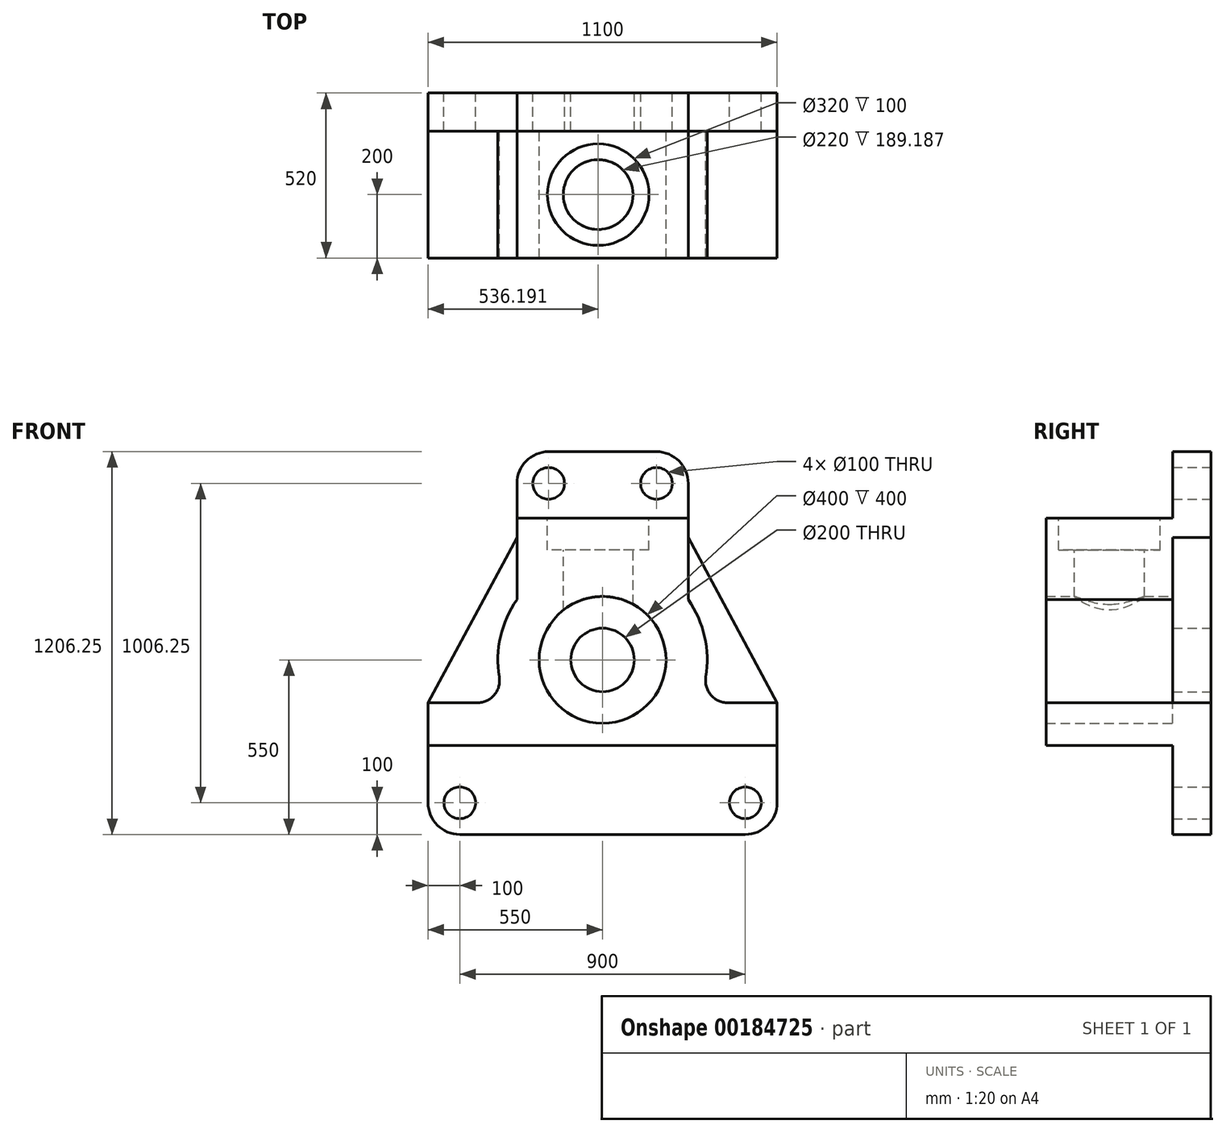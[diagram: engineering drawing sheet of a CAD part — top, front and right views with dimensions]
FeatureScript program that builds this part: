
annotation { "Feature Type Name" : "Feature", "Feature Type Description" : "" }
export const myFeature = defineFeature(function(context is Context, id is Id, definition is map)
    precondition{}
    {
        {
            var Q0;
            Q0=qCreatedBy(makeId("Front.planeOp"),FACE);
            var sketch = newSketch(context, id + "F0", { "sketchPlane" : qUnion([Q0])});
            skLineSegment(sketch, "E0", {"start": v(0, 1430) * mm, "end": v(0, -470) * mm, "construction": true});
            skLineSegment(sketch, "E1", {"start": v(450, 0) * mm, "end": v(60, 0) * mm});
            skLineSegment(sketch, "E2", {"start": v(-60, 0) * mm, "end": v(-60, 280) * mm});
            skLineSegment(sketch, "E3", {"start": v(60, 0) * mm, "end": v(60, 280) * mm});
            skArc(sketch, "E4", {"start": v(-450, 0) * mm, "mid": v(-520.71, 29.29) * mm, "end": v(-550, 100) * mm});
            skArc(sketch, "E5", {"start": v(450, 0) * mm, "mid": v(520.71, 29.29) * mm, "end": v(550, 100) * mm});
            skCircle(sketch, "E6", {"center": v(-450, 100) * mm, "radius": 50 * mm});
            skCircle(sketch, "E7", {"center": v(450, 100) * mm, "radius": 50 * mm});
            skLineSegment(sketch, "E8", {"start": v(-550, 100) * mm, "end": v(-550, 280) * mm});
            skLineSegment(sketch, "E9", {"start": v(550, 100) * mm, "end": v(550, 280) * mm});
            skLineSegment(sketch, "E10", {"start": v(-60, 280) * mm, "end": v(-550, 280) * mm});
            skLineSegment(sketch, "E11", {"start": v(60, 280) * mm, "end": v(550, 280) * mm});
            skLineSegment(sketch, "E12", {"start": v(-60, 280) * mm, "end": v(60, 280) * mm});
            skCircle(sketch, "E13", {"center": v(0, 550) * mm, "radius": 100 * mm});
            skCircle(sketch, "E14", {"center": v(0, 550) * mm, "radius": 200 * mm});
            skLineSegment(sketch, "E15", {"start": v(-550, 280) * mm, "end": v(-550, 415) * mm});
            skArc(sketch, "E16", {"start": v(325.61, 496.38) * mm, "mid": v(321.7, 623.52) * mm, "end": v(270, 739.74) * mm});
            skLineSegment(sketch, "E17", {"start": v(-550, 415) * mm, "end": v(-394.68, 415) * mm});
            skArc(sketch, "E18", {"start": v(-394.68, 415) * mm, "mid": v(-341.32, 439.7) * mm, "end": v(-325.61, 496.37) * mm});
            skLineSegment(sketch, "E19.MirrorCS", {"start": v(550, 280) * mm, "end": v(550, 415) * mm});
            skLineSegment(sketch, "E20.MirrorCS", {"start": v(550, 415) * mm, "end": v(394.68, 415) * mm});
            skArc(sketch, "E21.MirrorCS", {"start": v(394.68, 415) * mm, "mid": v(341.32, 439.7) * mm, "end": v(325.61, 496.37) * mm});
            skLineSegment(sketch, "E22", {"start": v(270, 996.25) * mm, "end": v(-270, 996.25) * mm});
            skArc(sketch, "E23", {"start": v(-170, 1206.25) * mm, "mid": v(-240.71, 1176.96) * mm, "end": v(-270, 1106.25) * mm});
            skArc(sketch, "E24.MirrorCS", {"start": v(170, 1206.25) * mm, "mid": v(240.71, 1176.96) * mm, "end": v(270, 1106.25) * mm});
            skLineSegment(sketch, "E25", {"start": v(-270, 1106.25) * mm, "end": v(-270, 996.25) * mm});
            skLineSegment(sketch, "E26", {"start": v(270, 1106.25) * mm, "end": v(270, 996.25) * mm});
            skCircle(sketch, "E27", {"center": v(-170, 1106.25) * mm, "radius": 50 * mm});
            skCircle(sketch, "E28.MirrorC", {"center": v(170, 1106.25) * mm, "radius": 50 * mm});
            skLineSegment(sketch, "E29", {"start": v(-270, 996.25) * mm, "end": v(-270, 739.74) * mm});
            skLineSegment(sketch, "E30", {"start": v(270, 996.25) * mm, "end": v(270, 739.74) * mm});
            skArc(sketch, "E31.trimOffspring", {"start": v(-270, 739.74) * mm, "mid": v(-321.7, 623.52) * mm, "end": v(-325.61, 496.37) * mm});
            skLineSegment(sketch, "E32", {"start": v(170, 1206.25) * mm, "end": v(-170, 1206.25) * mm});
            skLineSegment(sketch, "E33.trimOffspring", {"start": v(-60, 0) * mm, "end": v(-450, 0) * mm});
            skLineSegment(sketch, "E34", {"start": v(60, 0) * mm, "end": v(-60, 0) * mm});
            skLineSegment(sketch, "E35", {"start": v(-270, 936.25) * mm, "end": v(-550, 415) * mm});
            skLineSegment(sketch, "E36.MirrorCS", {"start": v(270, 936.25) * mm, "end": v(550, 415) * mm});
            skSolve(sketch);
        }
        {
            var Q0;
            Q0=makeQuery(id+"F0.imprint","IMPRINT",FACE,{"disambiguationData":[TD([[makeQuery(id+"F0.imprint","IMPRINT",EDGE,{"derivedFrom":sQuery(id+"F0.wireOp",EDGE,"E10")}),-1.0]])]});
            extrude(context, id + "F1", {"entities" : qUnion([Q0]), "depth" : 520 * mm});
        }
        {
            var Q0;
            Q0 = qSketchRegion(id + "F0", true);
            extrude(context, id + "F2", {"entities" : qUnion([Q0]), "operationType" : NewBodyOperationType.ADD, "depth" : 120 * mm});
        }
        {
            var Q0;
            Q0=makeQuery(id+"F0.imprint","IMPRINT",FACE,{"disambiguationData":[TD([[makeQuery(id+"F0.imprint","IMPRINT",EDGE,{"derivedFrom":sQuery(id+"F0.wireOp",EDGE,"E13")}),-1.0]])]});
            extrude(context, id + "F3", {"entities" : qUnion([Q0]), "operationType" : NewBodyOperationType.ADD, "depth" : 120 * mm});
        }
        {
            var Q0;
            Q0=makeQuery(id+"F1.opExtrude","SWEPT_FACE",FACE,{"disambiguationData":[OSD([sQuery(id+"F0.wireOp",EDGE,"E22")])]});
            var sketch = newSketch(context, id + "F4", { "sketchPlane" : qUnion([Q0])});
            skLineSegment(sketch, "E37", {"start": v(-13.8, -120) * mm, "end": v(-13.8, -520) * mm});
            skCircle(sketch, "E38", {"center": v(-13.8, -320) * mm, "radius": 110 * mm});
            skCircle(sketch, "E39", {"center": v(-13.8, -320) * mm, "radius": 160 * mm});
            skSolve(sketch);
        }
        {
            var Q0;
            {var subQ0=sQuery(id+"F4.wireOp",EDGE,"E39");var subQ1=sQuery(id+"F4.wireOp",EDGE,"E37");var subQ2=makeQuery(id+"F4.imprint","INTERSECT",VERTEX,{"disambiguationData":[OD(0.0)],"derivedFrom":[subQ1,subQ0]});Q0=makeQuery(id+"F4.imprint","IMPRINT",FACE,{"disambiguationData":[TD([[makeQuery(id+"F4.imprint","IMPRINT",EDGE,{"disambiguationData":[TD([[subQ2,-1.0]])],"derivedFrom":subQ1}),1.0]])]});}
            var Q1;
            {var subQ0=sQuery(id+"F4.wireOp",EDGE,"E39");var subQ1=sQuery(id+"F4.wireOp",EDGE,"E37");var subQ2=makeQuery(id+"F4.imprint","INTERSECT",VERTEX,{"disambiguationData":[OD(0.0)],"derivedFrom":[subQ1,subQ0]});Q1=makeQuery(id+"F4.imprint","IMPRINT",FACE,{"disambiguationData":[TD([[makeQuery(id+"F4.imprint","IMPRINT",EDGE,{"disambiguationData":[TD([[subQ2,-1.0]])],"derivedFrom":subQ1}),-1.0]])]});}
            extrude(context, id + "F5", {"entities" : qUnion([Q0, Q1]), "operationType" : NewBodyOperationType.REMOVE, "oppositeDirection" : true, "depth" : 100 * mm});
        }
        {
            var Q0;
            Q0=makeQuery(id+"F5.boolean.opBoolean","SPLIT",FACE,{"disambiguationData":[TD([makeQuery(id+"F5.opExtrude","SWEPT_FACE",FACE,{"disambiguationData":[OSD([sQuery(id+"F4.wireOp",EDGE,"E38")])]})])],"derivedFrom":makeQuery(id+"F1.opExtrude","SWEPT_FACE",FACE,{"disambiguationData":[OSD([sQuery(id+"F0.wireOp",EDGE,"E22")])]})});
            var sketch = newSketch(context, id + "F6", { "sketchPlane" : qUnion([Q0])});
            skSolve(sketch);
        }
        {
            var Q0;
            Q0=makeQuery(id+"F6.imprint","IMPRINT",FACE,{"disambiguationData":[TD([[makeQuery(id+"F6.imprint","IMPRINT",EDGE,{"derivedFrom":makeQuery(id+"F5.boolean.opBoolean","COPY",EDGE,{"derivedFrom":makeQuery(id+"F5.opExtrude","CAP_EDGE",EDGE,{"disambiguationData":[OSD([sQuery(id+"F4.wireOp",EDGE,"E38")])],"isStart":true})})}),1.0]])]});
            extrude(context, id + "F7", {"entities" : qUnion([Q0]), "operationType" : NewBodyOperationType.REMOVE, "endBound" : BoundingType.UP_TO_NEXT, "oppositeDirection" : true, "depth" : 25 * mm});
        }
    });
